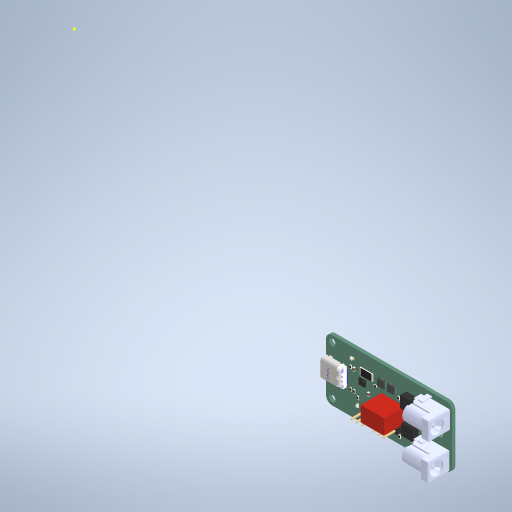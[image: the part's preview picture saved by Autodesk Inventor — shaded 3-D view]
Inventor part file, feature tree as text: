
AUTODESK INVENTOR PART (.ipt)
format: ipt  version: 2023 (Build 270158000, 158)  size: 4,319,744 bytes
history: native  units: in
note: dims shown in document units (in); Inventor stores cm internally (conversion verified against a paired STEP export)
features: sketch x2, extrude x1, projected_geometry x1
ambient origin geometry x8: Origin, YZ Plane, XZ Plane, XY Plane, X Axis, Y Axis, Z Axis, Center Point
bodies: Solid1 (feature_tree), Solid2 (feature_tree), Solid3 (feature_tree), Solid4 (feature_tree), Solid5 (feature_tree), Solid6 (feature_tree), Solid7 (feature_tree), Solid8 (feature_tree), Solid9 (feature_tree), Solid10 (feature_tree), Solid11 (feature_tree), Solid12 (feature_tree), Solid13 (feature_tree), Solid14 (feature_tree), Solid15 (feature_tree), Solid16 (feature_tree), Solid17 (feature_tree), Solid18 (feature_tree), Solid19 (feature_tree), Solid20 (feature_tree), Solid21 (feature_tree), Solid22 (feature_tree), Solid23 (feature_tree), Solid24 (feature_tree), Solid25 (feature_tree), Solid26 (feature_tree), Solid27 (feature_tree), Solid28 (feature_tree), Solid29 (feature_tree), Solid30 (feature_tree), Solid31 (feature_tree), Solid32 (feature_tree), Solid33 (feature_tree), Solid34 (feature_tree), Solid35 (feature_tree), Solid36 (feature_tree), Solid37 (feature_tree), Solid38 (feature_tree), Solid39 (feature_tree), Solid40 (feature_tree), Solid41 (feature_tree), Solid42 (feature_tree), Solid43 (feature_tree), Solid44 (feature_tree), Solid45 (feature_tree), Solid46 (feature_tree), Solid47 (feature_tree), Solid48 (feature_tree), Solid49 (feature_tree), Solid50 (feature_tree), Solid51 (feature_tree), Solid52 (feature_tree), Solid53 (feature_tree), Solid54 (feature_tree), Solid55 (feature_tree), Solid56 (feature_tree), Solid57 (feature_tree), Solid58 (feature_tree)
feature tree (4):
  sketch  "Sketch1"  dims[d0=0.2362in d1=0.2362in]
  extrude  "Extrusion1"  Depth=0.2362in
  sketch  "Sketch2"  dims[d2=0.126in d3=0.126in d4=0.126in d5=0.5709in d6=2.2047in d7=0.3563in d8=0.0in]
  projected_geometry  "Projected Loop1"
